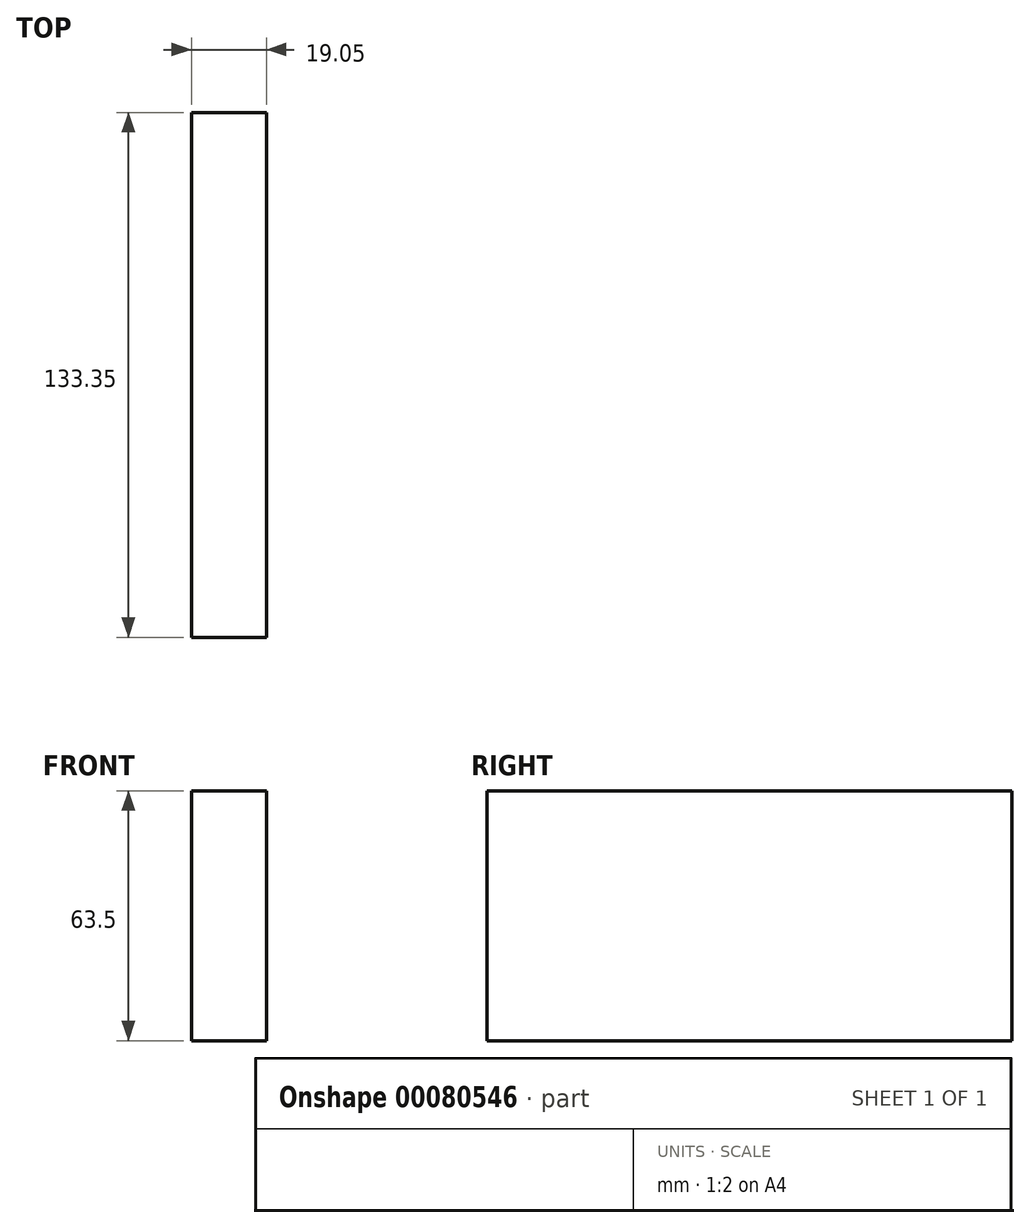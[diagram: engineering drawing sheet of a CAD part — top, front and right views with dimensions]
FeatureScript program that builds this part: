
annotation { "Feature Type Name" : "Feature", "Feature Type Description" : "" }
export const myFeature = defineFeature(function(context is Context, id is Id, definition is map)
    precondition{}
    {
        {
            var Q0;
            Q0=qCreatedBy(makeId("Right.planeOp"),FACE);
            var sketch = newSketch(context, id + "F0", { "sketchPlane" : qUnion([Q0])});
            skLineSegment(sketch, "E0.bottom", {"start": v(0, 0) * mm, "end": v(-133.35, 0) * mm});
            skLineSegment(sketch, "E0.top", {"start": v(0, -63.5) * mm, "end": v(-133.35, -63.5) * mm});
            skLineSegment(sketch, "E0.left", {"start": v(0, 0) * mm, "end": v(0, -63.5) * mm});
            skLineSegment(sketch, "E0.right", {"start": v(-133.35, 0) * mm, "end": v(-133.35, -63.5) * mm});
            skSolve(sketch);
        }
        {
            var Q0;
            Q0=makeQuery(id+"F0.imprint","IMPRINT",FACE,{"disambiguationData":[TD([[makeQuery(id+"F0.imprint","IMPRINT",EDGE,{"derivedFrom":sQuery(id+"F0.wireOp",EDGE,"E0.bottom")}),1.0]])]});
            extrude(context, id + "F1", {"entities" : qUnion([Q0]), "depth" : 19.05 * mm});
        }
    });
